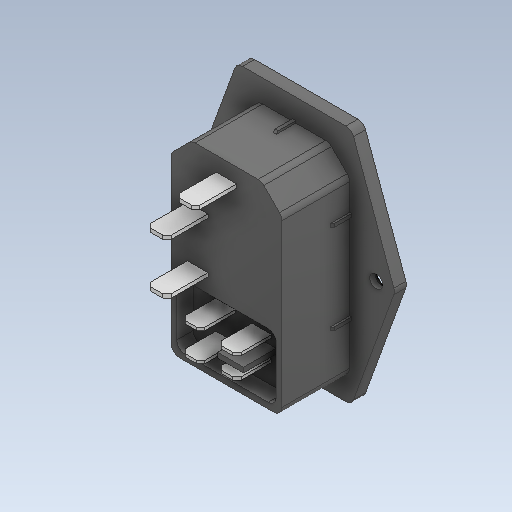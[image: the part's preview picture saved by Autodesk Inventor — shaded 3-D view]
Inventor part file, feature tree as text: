
AUTODESK INVENTOR PART (.ipt)
format: ipt  version: 2020 (Build 240168000, 168)  size: 259,584 bytes
history: native  units: in
note: dims shown in document units (in); Inventor stores cm internally (conversion verified against a paired STEP export)
features: chamfer x1
ambient origin geometry x8: Origin, YZ Plane, XZ Plane, XY Plane, X Axis, Y Axis, Z Axis, Center Point
bodies: Solid1 (feature_tree)
feature tree (1):
  chamfer  "Chamfer4"  [1 undecoded]
note: 1 required parameter value undecoded (feature->parameter linkage not recoverable at this tier; creation-order binding heuristic only, values carry confidence <= 0.55)
